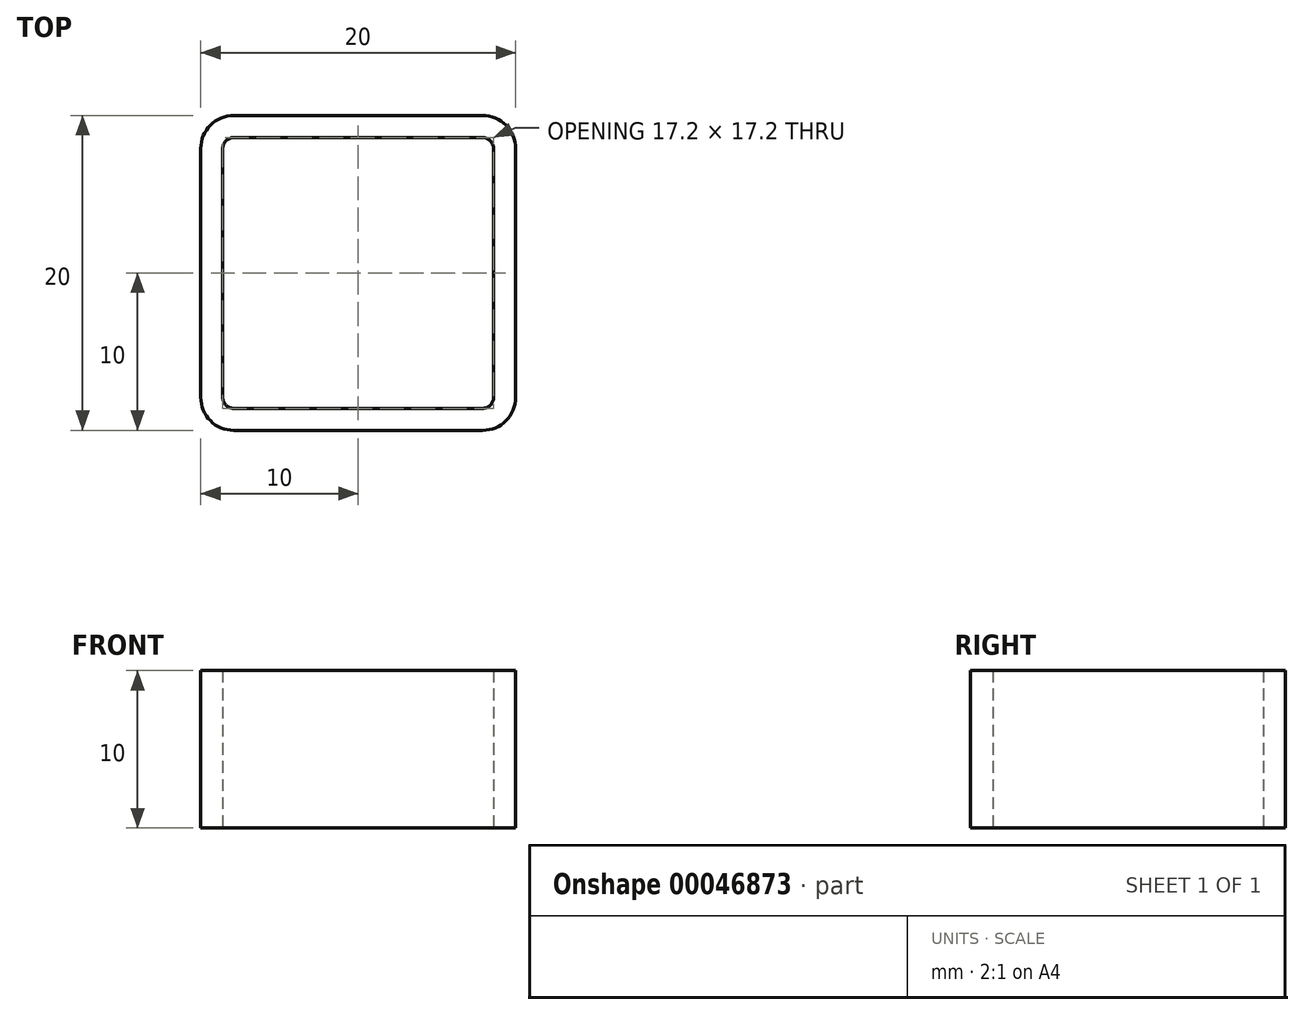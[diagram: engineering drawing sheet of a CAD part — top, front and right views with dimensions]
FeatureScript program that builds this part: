
annotation { "Feature Type Name" : "Feature", "Feature Type Description" : "" }
export const myFeature = defineFeature(function(context is Context, id is Id, definition is map)
    precondition{}
    {
        {
            var Q0;
            Q0=qCreatedBy(makeId("Top.planeOp"),FACE);
            var sketch = newSketch(context, id + "F0", { "sketchPlane" : qUnion([Q0])});
            skLineSegment(sketch, "E0.rect.bottom", {"start": v(10, 10) * mm, "end": v(-10, 10) * mm});
            skLineSegment(sketch, "E0.rect.top", {"start": v(10, -10) * mm, "end": v(-10, -10) * mm});
            skLineSegment(sketch, "E0.rect.left", {"start": v(10, 10) * mm, "end": v(10, -10) * mm});
            skLineSegment(sketch, "E0.rect.right", {"start": v(-10, 10) * mm, "end": v(-10, -10) * mm});
            skPoint(sketch, "E0.rect.middle", {"position": v(0, 0) * mm});
            skLineSegment(sketch, "E1.rect.bottom", {"start": v(8.6, 8.6) * mm, "end": v(-8.6, 8.6) * mm});
            skLineSegment(sketch, "E1.rect.top", {"start": v(8.6, -8.6) * mm, "end": v(-8.6, -8.6) * mm});
            skLineSegment(sketch, "E1.rect.left", {"start": v(8.6, 8.6) * mm, "end": v(8.6, -8.6) * mm});
            skLineSegment(sketch, "E1.rect.right", {"start": v(-8.6, 8.6) * mm, "end": v(-8.6, -8.6) * mm});
            skSolve(sketch);
        }
        {
            var Q0;
            Q0=makeQuery(id+"F0.imprint","IMPRINT",FACE,{"disambiguationData":[TD([[makeQuery(id+"F0.imprint","IMPRINT",EDGE,{"derivedFrom":sQuery(id+"F0.wireOp",EDGE,"E0.rect.bottom")}),1.0]])]});
            extrude(context, id + "F1", {"entities" : qUnion([Q0]), "depth" : 10 * mm});
        }
        {
            var Q0;
            Q0=makeQuery(id+"F1.opExtrude","SWEPT_EDGE",EDGE,{"disambiguationData":[OSD([sQuery(id+"F0.wireOp",EDGE,"E0.rect.top"),sQuery(id+"F0.wireOp",EDGE,"E0.rect.right")])]});
            var Q1;
            Q1=makeQuery(id+"F1.opExtrude","SWEPT_EDGE",EDGE,{"disambiguationData":[OSD([sQuery(id+"F0.wireOp",EDGE,"E0.rect.top"),sQuery(id+"F0.wireOp",EDGE,"E0.rect.left")])]});
            var Q2;
            Q2=makeQuery(id+"F1.opExtrude","SWEPT_EDGE",EDGE,{"disambiguationData":[OSD([sQuery(id+"F0.wireOp",EDGE,"E0.rect.bottom"),sQuery(id+"F0.wireOp",EDGE,"E0.rect.left")])]});
            fillet(context, id + "F2", {"entities" : qUnion([Q0, Q1, Q2]), "radius" : 2.1 * mm, "tangentPropagation" : true, "allowEdgeOverflow" : false});
        }
        {
            var Q0;
            Q0=makeQuery(id+"F1.opExtrude","SWEPT_EDGE",EDGE,{"disambiguationData":[OSD([sQuery(id+"F0.wireOp",EDGE,"E0.rect.bottom"),sQuery(id+"F0.wireOp",EDGE,"E0.rect.right")])]});
            fillet(context, id + "F3", {"entities" : qUnion([Q0]), "radius" : 2.1 * mm, "tangentPropagation" : true, "allowEdgeOverflow" : false});
        }
        {
            var Q0;
            Q0=makeQuery(id+"F1.opExtrude","SWEPT_EDGE",EDGE,{"disambiguationData":[OSD([sQuery(id+"F0.wireOp",EDGE,"E1.rect.bottom"),sQuery(id+"F0.wireOp",EDGE,"E1.rect.right")])]});
            fillet(context, id + "F4", {"entities" : qUnion([Q0]), "radius" : 0.7 * mm, "tangentPropagation" : true, "allowEdgeOverflow" : false});
        }
        {
            var Q0;
            Q0=makeQuery(id+"F1.opExtrude","SWEPT_EDGE",EDGE,{"disambiguationData":[OSD([sQuery(id+"F0.wireOp",EDGE,"E1.rect.top"),sQuery(id+"F0.wireOp",EDGE,"E1.rect.right")])]});
            fillet(context, id + "F5", {"entities" : qUnion([Q0]), "radius" : 0.7 * mm, "tangentPropagation" : true, "allowEdgeOverflow" : false});
        }
        {
            var Q0;
            Q0=makeQuery(id+"F1.opExtrude","SWEPT_EDGE",EDGE,{"disambiguationData":[OSD([sQuery(id+"F0.wireOp",EDGE,"E1.rect.top"),sQuery(id+"F0.wireOp",EDGE,"E1.rect.left")])]});
            fillet(context, id + "F6", {"entities" : qUnion([Q0]), "radius" : 0.7 * mm, "tangentPropagation" : true, "allowEdgeOverflow" : false});
        }
        {
            var Q0;
            Q0=makeQuery(id+"F1.opExtrude","SWEPT_EDGE",EDGE,{"disambiguationData":[OSD([sQuery(id+"F0.wireOp",EDGE,"E1.rect.bottom"),sQuery(id+"F0.wireOp",EDGE,"E1.rect.left")])]});
            fillet(context, id + "F7", {"entities" : qUnion([Q0]), "radius" : 0.7 * mm, "tangentPropagation" : true, "allowEdgeOverflow" : false});
        }
    });
